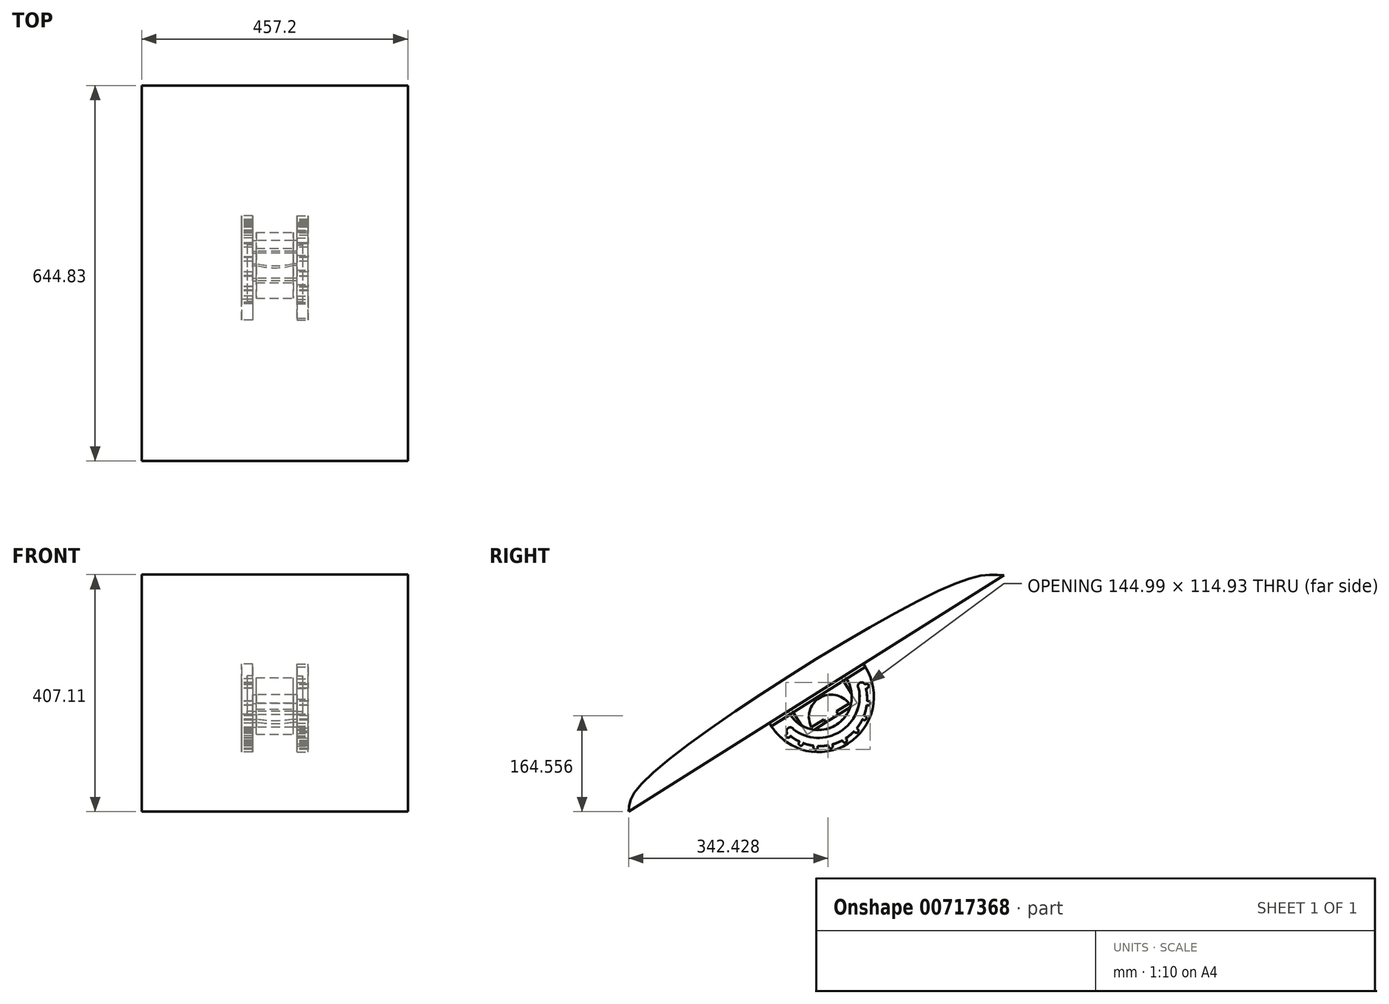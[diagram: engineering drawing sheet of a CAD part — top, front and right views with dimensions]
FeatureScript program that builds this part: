
annotation { "Feature Type Name" : "Feature", "Feature Type Description" : "" }
export const myFeature = defineFeature(function(context is Context, id is Id, definition is map)
    precondition{}
    {
        {
            var Q0;
            Q0=qCreatedBy(makeId("Right.planeOp"),FACE);
            var sketch = newSketch(context, id + "F0", { "sketchPlane" : qUnion([Q0])});
            skLineSegment(sketch, "E0", {"start": v(0, 0) * mm, "end": v(-644.83, -406) * mm});
            skFitSpline(sketch, "E1", {"points": [v(-644.83, -406) * mm, v(-622.98, -358.63) * mm, v(-89.62, -16.58) * mm, v(0, 0) * mm], "startDerivative": vector(4.72, 213.44) * mm, "endDerivative": vector(267.13, -25.02) * mm});
            skSolve(sketch);
        }
        {
            var Q0;
            Q0 = qSketchRegion(id + "F0", true);
            extrude(context, id + "F1", {"entities" : qUnion([Q0]), "depth" : 457.2 * mm, "offsetDistance" : 25.4 * mm});
        }
        {
            var Q0;
            Q0=makeQuery(id+"F1.opExtrude","SWEPT_FACE",FACE,{"disambiguationData":[OSD([sQuery(id+"F0.wireOp",EDGE,"E0")])]});
            var sketch = newSketch(context, id + "F2", { "sketchPlane" : qUnion([Q0])});
            skLineSegment(sketch, "E2", {"start": v(228.6, 0) * mm, "end": v(228.6, 762) * mm, "construction": true});
            skLineSegment(sketch, "E3", {"start": v(457.2, 381) * mm, "end": v(0, 381) * mm, "construction": true});
            skLineSegment(sketch, "E4.bottom", {"start": v(196.85, 431.8) * mm, "end": v(260.35, 431.8) * mm});
            skLineSegment(sketch, "E4.top", {"start": v(196.85, 330.2) * mm, "end": v(260.35, 330.2) * mm});
            skLineSegment(sketch, "E4.left", {"start": v(196.85, 431.8) * mm, "end": v(196.85, 330.2) * mm});
            skLineSegment(sketch, "E4.right", {"start": v(260.35, 431.8) * mm, "end": v(260.35, 330.2) * mm});
            skPoint(sketch, "E4.middle", {"position": v(228.6, 381) * mm});
            skSolve(sketch);
        }
        {
            var Q0;
            Q0=makeQuery(id+"F2.imprint","IMPRINT",FACE,{"disambiguationData":[TD([[makeQuery(id+"F2.imprint","IMPRINT",EDGE,{"derivedFrom":sQuery(id+"F2.wireOp",EDGE,"E4.bottom")}),-1.0]])]});
            extrude(context, id + "F3", {"entities" : qUnion([Q0]), "operationType" : NewBodyOperationType.ADD, "depth" : 50.8 * mm, "offsetDistance" : 25.4 * mm});
        }
        {
            var Q0;
            Q0=makeQuery(id+"F3.opExtrude","SWEPT_FACE",FACE,{"disambiguationData":[OSD([sQuery(id+"F2.wireOp",EDGE,"E4.left")])]});
            var sketch = newSketch(context, id + "F4", { "sketchPlane" : qUnion([Q0])});
            skLineSegment(sketch, "E5", {"start": v(252.36, -218.92) * mm, "end": v(284.6, -239.22) * mm, "construction": true});
            skLineSegment(sketch, "E6", {"start": v(338.34, -273.06) * mm, "end": v(306.1, -252.76) * mm, "construction": true});
            skLineSegment(sketch, "E7", {"start": v(284.6, -239.22) * mm, "end": v(306.1, -252.76) * mm});
            skLineSegment(sketch, "E8", {"start": v(306.1, -252.76) * mm, "end": v(309.48, -247.38) * mm});
            skLineSegment(sketch, "E9", {"start": v(284.6, -239.22) * mm, "end": v(287.98, -233.85) * mm});
            skLineSegment(sketch, "E10", {"start": v(309.48, -247.38) * mm, "end": v(330.97, -260.92) * mm});
            skLineSegment(sketch, "E11", {"start": v(287.98, -233.85) * mm, "end": v(266.49, -220.32) * mm});
            skArc(sketch, "E12", {"start": v(330.97, -260.92) * mm, "mid": v(317.44, -210.9) * mm, "end": v(266.49, -220.32) * mm});
            skSolve(sketch);
        }
        {
            var Q0;
            Q0=makeQuery(id+"F4.imprint","IMPRINT",FACE,{"disambiguationData":[TD([[makeQuery(id+"F4.imprint","IMPRINT",EDGE,{"derivedFrom":sQuery(id+"F4.wireOp",EDGE,"E7")}),-1.0]])]});
            extrude(context, id + "F5", {"entities" : qUnion([Q0]), "operationType" : NewBodyOperationType.REMOVE, "oppositeDirection" : true, "depth" : 127 * mm, "offsetDistance" : 25.4 * mm});
        }
        {
            var Q0;
            Q0=makeQuery(id+"F3.opExtrude","SWEPT_FACE",FACE,{"disambiguationData":[OSD([sQuery(id+"F2.wireOp",EDGE,"E4.left")])]});
            var sketch = newSketch(context, id + "F6", { "sketchPlane" : qUnion([Q0])});
            skLineSegment(sketch, "E13", {"start": v(284.6, -239.22) * mm, "end": v(306.1, -252.76) * mm});
            skSolve(sketch);
        }
        {
            var Q0;
            {var subQ1=sQuery(id+"F2.wireOp",EDGE,"E4.left");Q0=makeQuery(id+"F6.imprint","IMPRINT",FACE,{"disambiguationData":[TD([[makeQuery(id+"F6.imprint","IMPRINT",EDGE,{"derivedFrom":makeQuery(id+"F3.opExtrude","CAP_EDGE",EDGE,{"disambiguationData":[OSD([subQ1])],"isStart":true})}),1.0]])]});}
            var Q1;
            Q1=makeQuery(id+"F6.imprint","IMPRINT",FACE,{"disambiguationData":[TD([[makeQuery(id+"F6.imprint","IMPRINT",EDGE,{"derivedFrom":sQuery(id+"F6.wireOp",EDGE,"E13")}),1.0]])]});
            extrude(context, id + "F7", {"entities" : qUnion([Q0, Q1]), "operationType" : NewBodyOperationType.ADD, "depth" : 6.35 * mm, "offsetDistance" : 25.4 * mm});
        }
        {
            var Q0;
            Q0=makeQuery(id+"F3.opExtrude","SWEPT_FACE",FACE,{"disambiguationData":[OSD([sQuery(id+"F2.wireOp",EDGE,"E4.right")])]});
            var sketch = newSketch(context, id + "F8", { "sketchPlane" : qUnion([Q0])});
            skLineSegment(sketch, "E14", {"start": v(-306.1, -252.76) * mm, "end": v(-284.6, -239.22) * mm});
            skSolve(sketch);
        }
        {
            var Q0;
            {var subQ1=sQuery(id+"F2.wireOp",EDGE,"E4.right");Q0=makeQuery(id+"F8.imprint","IMPRINT",FACE,{"disambiguationData":[TD([[makeQuery(id+"F8.imprint","IMPRINT",EDGE,{"derivedFrom":makeQuery(id+"F3.opExtrude","CAP_EDGE",EDGE,{"disambiguationData":[OSD([subQ1])],"isStart":true})}),-1.0]])]});}
            var Q1;
            Q1=makeQuery(id+"F8.imprint","IMPRINT",FACE,{"disambiguationData":[TD([[makeQuery(id+"F8.imprint","IMPRINT",EDGE,{"derivedFrom":sQuery(id+"F8.wireOp",EDGE,"E14")}),1.0]])]});
            extrude(context, id + "F9", {"entities" : qUnion([Q0, Q1]), "operationType" : NewBodyOperationType.ADD, "depth" : 6.35 * mm, "offsetDistance" : 25.4 * mm});
        }
        {
            var Q0;
            {var subQ0=sQuery(id+"F2.wireOp",EDGE,"E4.right");var subQ1=sQuery(id+"F2.wireOp",EDGE,"E4.left");var subQ2=sQuery(id+"F2.wireOp",EDGE,"E4.top");var subQ5=sQuery(id+"F2.wireOp",EDGE,"E4.bottom");var subQ6=makeQuery(id+"F3.opExtrude","CAP_FACE",FACE,{"disambiguationData":[OSD([subQ5,subQ2,subQ1,subQ0])],"isStart":false});Q0=makeQuery(id+"F9.boolean.opBoolean","MERGE",FACE,{"derivedFrom":[makeQuery(id+"F7.boolean.opBoolean","MERGE",FACE,{"derivedFrom":[makeQuery(id+"F5.boolean.opBoolean","SPLIT",FACE,{"disambiguationData":[TD([makeQuery(id+"F3.opExtrude","SWEPT_FACE",FACE,{"disambiguationData":[OSD([subQ5])]})])],"derivedFrom":subQ6}),makeQuery(id+"F5.boolean.opBoolean","SPLIT",FACE,{"disambiguationData":[TD([makeQuery(id+"F3.opExtrude","SWEPT_FACE",FACE,{"disambiguationData":[OSD([subQ2])]})])],"derivedFrom":subQ6}),makeQuery(id+"F7.opExtrude","SWEPT_FACE",FACE,{"disambiguationData":[OSD([subQ1,sQuery(id+"F6.wireOp",EDGE,"E13")])]})]}),makeQuery(id+"F9.opExtrude","SWEPT_FACE",FACE,{"disambiguationData":[OSD([subQ0,sQuery(id+"F8.wireOp",EDGE,"E14")])]})]});}
            var sketch = newSketch(context, id + "F10", { "sketchPlane" : qUnion([Q0])});
            skArc(sketch, "E15", {"start": v(196.85, 368.3) * mm, "mid": v(228.6, 364.38) * mm, "end": v(260.35, 368.3) * mm});
            skArc(sketch, "E16", {"start": v(260.35, 393.7) * mm, "mid": v(228.6, 398.67) * mm, "end": v(196.85, 393.7) * mm});
            skSolve(sketch);
        }
        {
            var Q0;
            Q0=makeQuery(id+"F10.imprint","IMPRINT",FACE,{"disambiguationData":[TD([[makeQuery(id+"F10.imprint","IMPRINT",EDGE,{"derivedFrom":sQuery(id+"F10.wireOp",EDGE,"E15")}),1.0]])]});
            var Q1;
            Q1=makeQuery(id+"F10.imprint","IMPRINT",FACE,{"disambiguationData":[TD([[makeQuery(id+"F10.imprint","IMPRINT",EDGE,{"derivedFrom":sQuery(id+"F10.wireOp",EDGE,"E16")}),1.0]])]});
            extrude(context, id + "F11", {"entities" : qUnion([Q0, Q1]), "operationType" : NewBodyOperationType.REMOVE, "oppositeDirection" : true, "depth" : 7.62 * mm, "offsetDistance" : 25.4 * mm});
        }
        {
            var Q0;
            Q0=makeQuery(id+"F1.opExtrude","SWEPT_FACE",FACE,{"disambiguationData":[OSD([sQuery(id+"F0.wireOp",EDGE,"E0")])]});
            var sketch = newSketch(context, id + "F12", { "sketchPlane" : qUnion([Q0])});
            skLineSegment(sketch, "E17", {"start": v(266.7, 330.2) * mm, "end": v(266.7, 323.85) * mm, "construction": true});
            skLineSegment(sketch, "E18", {"start": v(266.7, 431.8) * mm, "end": v(266.7, 438.15) * mm, "construction": true});
            skLineSegment(sketch, "E19", {"start": v(190.5, 431.8) * mm, "end": v(190.5, 438.15) * mm, "construction": true});
            skLineSegment(sketch, "E20", {"start": v(190.5, 330.2) * mm, "end": v(190.5, 323.85) * mm, "construction": true});
            skLineSegment(sketch, "E21.bottom", {"start": v(266.7, 323.85) * mm, "end": v(285.75, 323.85) * mm});
            skLineSegment(sketch, "E21.top", {"start": v(266.7, 285.75) * mm, "end": v(285.75, 285.75) * mm});
            skLineSegment(sketch, "E21.left", {"start": v(266.7, 323.85) * mm, "end": v(266.7, 285.75) * mm});
            skLineSegment(sketch, "E21.right", {"start": v(285.75, 323.85) * mm, "end": v(285.75, 285.75) * mm});
            skLineSegment(sketch, "E22.bottom", {"start": v(190.5, 323.85) * mm, "end": v(171.45, 323.85) * mm});
            skLineSegment(sketch, "E22.top", {"start": v(190.5, 285.75) * mm, "end": v(171.45, 285.75) * mm});
            skLineSegment(sketch, "E22.left", {"start": v(190.5, 323.85) * mm, "end": v(190.5, 285.75) * mm});
            skLineSegment(sketch, "E22.right", {"start": v(171.45, 323.85) * mm, "end": v(171.45, 285.75) * mm});
            skLineSegment(sketch, "E23.bottom", {"start": v(266.7, 438.15) * mm, "end": v(285.75, 438.15) * mm});
            skLineSegment(sketch, "E23.top", {"start": v(266.7, 476.25) * mm, "end": v(285.75, 476.25) * mm});
            skLineSegment(sketch, "E23.left", {"start": v(266.7, 438.15) * mm, "end": v(266.7, 476.25) * mm});
            skLineSegment(sketch, "E23.right", {"start": v(285.75, 438.15) * mm, "end": v(285.75, 476.25) * mm});
            skPoint(sketch, "E24.oppositeSnap0", {"position": v(276.23, 476.25) * mm});
            skLineSegment(sketch, "E24.bottom", {"start": v(190.5, 438.15) * mm, "end": v(171.45, 438.15) * mm});
            skLineSegment(sketch, "E24.top", {"start": v(190.5, 476.25) * mm, "end": v(171.45, 476.25) * mm});
            skLineSegment(sketch, "E24.left", {"start": v(190.5, 438.15) * mm, "end": v(190.5, 476.25) * mm});
            skLineSegment(sketch, "E24.right", {"start": v(171.45, 438.15) * mm, "end": v(171.45, 476.25) * mm});
            skSolve(sketch);
        }
        {
            var Q0;
            Q0=makeQuery(id+"F12.imprint","IMPRINT",FACE,{"disambiguationData":[TD([[makeQuery(id+"F12.imprint","IMPRINT",EDGE,{"derivedFrom":sQuery(id+"F12.wireOp",EDGE,"E21.bottom")}),-1.0]])]});
            var Q1;
            Q1=makeQuery(id+"F12.imprint","IMPRINT",FACE,{"disambiguationData":[TD([[makeQuery(id+"F12.imprint","IMPRINT",EDGE,{"derivedFrom":sQuery(id+"F12.wireOp",EDGE,"E22.bottom")}),1.0]])]});
            var Q2;
            Q2=makeQuery(id+"F12.imprint","IMPRINT",FACE,{"disambiguationData":[TD([[makeQuery(id+"F12.imprint","IMPRINT",EDGE,{"derivedFrom":sQuery(id+"F12.wireOp",EDGE,"E24.bottom")}),-1.0]])]});
            var Q3;
            Q3=makeQuery(id+"F12.imprint","IMPRINT",FACE,{"disambiguationData":[TD([[makeQuery(id+"F12.imprint","IMPRINT",EDGE,{"derivedFrom":sQuery(id+"F12.wireOp",EDGE,"E23.bottom")}),1.0]])]});
            extrude(context, id + "F13", {"entities" : qUnion([Q0, Q1, Q2, Q3]), "operationType" : NewBodyOperationType.ADD, "depth" : 6.35 * mm, "offsetDistance" : 25.4 * mm});
        }
        {
            var Q0;
            Q0=makeQuery(id+"F1.opExtrude","SWEPT_FACE",FACE,{"disambiguationData":[OSD([sQuery(id+"F0.wireOp",EDGE,"E0")])]});
            var sketch = newSketch(context, id + "F14", { "sketchPlane" : qUnion([Q0])});
            skLineSegment(sketch, "E25", {"start": v(180.98, 323.85) * mm, "end": v(180.98, 438.15) * mm});
            skLineSegment(sketch, "E26", {"start": v(276.23, 323.85) * mm, "end": v(276.23, 438.15) * mm});
            skLineSegment(sketch, "E27", {"start": v(171.45, 438.15) * mm, "end": v(171.45, 323.85) * mm});
            skLineSegment(sketch, "E28", {"start": v(285.75, 438.15) * mm, "end": v(285.75, 323.85) * mm});
            skSolve(sketch);
        }
        {
            var Q0;
            {var subQ0=sQuery(id+"F14.wireOp",EDGE,"E26");Q0=makeQuery(id+"F14.imprint","IMPRINT",FACE,{"disambiguationData":[TD([[makeQuery(id+"F14.imprint","IMPRINT",EDGE,{"derivedFrom":subQ0}),-1.0]])]});}
            var Q1;
            {var subQ0=sQuery(id+"F14.wireOp",EDGE,"E25");Q1=makeQuery(id+"F14.imprint","IMPRINT",FACE,{"disambiguationData":[TD([[makeQuery(id+"F14.imprint","IMPRINT",EDGE,{"derivedFrom":subQ0}),1.0]])]});}
            extrude(context, id + "F15", {"entities" : qUnion([Q0, Q1]), "operationType" : NewBodyOperationType.ADD, "depth" : 6.35 * mm, "offsetDistance" : 25.4 * mm});
        }
        {
            var Q0;
            Q0=makeQuery(id+"F15.boolean.opBoolean","MERGE",FACE,{"derivedFrom":[makeQuery(id+"F13.opExtrude","SWEPT_FACE",FACE,{"disambiguationData":[OSD([sQuery(id+"F12.wireOp",EDGE,"E22.right")])]}),makeQuery(id+"F13.opExtrude","SWEPT_FACE",FACE,{"disambiguationData":[OSD([sQuery(id+"F12.wireOp",EDGE,"E24.right")])]}),makeQuery(id+"F15.opExtrude","SWEPT_FACE",FACE,{"disambiguationData":[OSD([sQuery(id+"F14.wireOp",EDGE,"E27")])]})]});
            var sketch = newSketch(context, id + "F16", { "sketchPlane" : qUnion([Q0])});
            skArc(sketch, "E29", {"start": v(270.41, -177.76) * mm, "mid": v(288.37, -256.78) * mm, "end": v(367.38, -238.82) * mm});
            skArc(sketch, "E30", {"start": v(238.43, -157.62) * mm, "mid": v(268.28, -288.98) * mm, "end": v(399.64, -259.13) * mm});
            skLineSegment(sketch, "E31", {"start": v(399.64, -259.13) * mm, "end": v(388.89, -252.36) * mm, "construction": true});
            skLineSegment(sketch, "E32", {"start": v(378.13, -245.59) * mm, "end": v(367.38, -238.82) * mm, "construction": true});
            skLineSegment(sketch, "E33", {"start": v(388.89, -252.36) * mm, "end": v(372.2, -271.52) * mm, "construction": true});
            skLineSegment(sketch, "E34", {"start": v(378.13, -245.59) * mm, "end": v(361.45, -264.74) * mm, "construction": true});
            skLineSegment(sketch, "E35", {"start": v(270.41, -177.76) * mm, "end": v(259.66, -171) * mm, "construction": true});
            skLineSegment(sketch, "E36", {"start": v(238.43, -157.62) * mm, "end": v(249.17, -164.4) * mm, "construction": true});
            skLineSegment(sketch, "E37", {"start": v(249.17, -164.4) * mm, "end": v(239.1, -187.71) * mm, "construction": true});
            skLineSegment(sketch, "E38", {"start": v(259.66, -171) * mm, "end": v(249.6, -194.32) * mm, "construction": true});
            skArc(sketch, "E39", {"start": v(249.6, -194.32) * mm, "mid": v(281.26, -268.07) * mm, "end": v(361.45, -264.74) * mm});
            skArc(sketch, "E40", {"start": v(239.1, -187.71) * mm, "mid": v(273.39, -280.87) * mm, "end": v(372.2, -271.52) * mm});
            skArc(sketch, "E41", {"start": v(372.2, -271.52) * mm, "mid": v(370.78, -261.85) * mm, "end": v(361.45, -264.74) * mm});
            skArc(sketch, "E42", {"start": v(249.6, -194.32) * mm, "mid": v(248.21, -184.89) * mm, "end": v(239.1, -187.71) * mm});
            skLineSegment(sketch, "E43", {"start": v(372.2, -271.52) * mm, "end": v(367.4, -275.66) * mm, "construction": true});
            skLineSegment(sketch, "E44", {"start": v(351.21, -285.7) * mm, "end": v(345.36, -288.17) * mm, "construction": true});
            skLineSegment(sketch, "E45", {"start": v(345.36, -288.17) * mm, "end": v(326.87, -292.74) * mm, "construction": true});
            skLineSegment(sketch, "E46", {"start": v(326.87, -292.74) * mm, "end": v(320.54, -293.29) * mm, "construction": true});
            skLineSegment(sketch, "E47", {"start": v(320.54, -293.29) * mm, "end": v(301.54, -291.95) * mm, "construction": true});
            skLineSegment(sketch, "E48", {"start": v(301.54, -291.95) * mm, "end": v(295.35, -290.52) * mm, "construction": true});
            skLineSegment(sketch, "E49", {"start": v(295.35, -290.52) * mm, "end": v(277.68, -283.4) * mm, "construction": true});
            skLineSegment(sketch, "E50", {"start": v(272.23, -280.13) * mm, "end": v(277.68, -283.4) * mm, "construction": true});
            skLineSegment(sketch, "E51", {"start": v(272.23, -280.13) * mm, "end": v(257.62, -267.91) * mm, "construction": true});
            skLineSegment(sketch, "E52", {"start": v(257.62, -267.91) * mm, "end": v(253.44, -263.13) * mm, "construction": true});
            skLineSegment(sketch, "E53", {"start": v(243.29, -247.01) * mm, "end": v(253.44, -263.13) * mm, "construction": true});
            skLineSegment(sketch, "E54", {"start": v(243.29, -247.01) * mm, "end": v(240.79, -241.18) * mm, "construction": true});
            skLineSegment(sketch, "E55", {"start": v(236.1, -222.71) * mm, "end": v(240.79, -241.18) * mm, "construction": true});
            skLineSegment(sketch, "E56", {"start": v(236.1, -222.71) * mm, "end": v(235.5, -216.4) * mm, "construction": true});
            skLineSegment(sketch, "E57", {"start": v(239.1, -187.71) * mm, "end": v(237.45, -193.84) * mm, "construction": true});
            skLineSegment(sketch, "E58", {"start": v(235.5, -216.4) * mm, "end": v(237.45, -193.84) * mm, "construction": true});
            skLineSegment(sketch, "E59", {"start": v(367.4, -275.66) * mm, "end": v(351.21, -285.7) * mm, "construction": true});
            skArc(sketch, "E60", {"start": v(367.4, -275.66) * mm, "mid": v(373.67, -278.07) * mm, "end": v(372.2, -271.52) * mm});
            skArc(sketch, "E61", {"start": v(345.36, -288.17) * mm, "mid": v(350.58, -292.39) * mm, "end": v(351.21, -285.7) * mm});
            skArc(sketch, "E62", {"start": v(320.54, -293.29) * mm, "mid": v(324.21, -298.9) * mm, "end": v(326.87, -292.74) * mm});
            skArc(sketch, "E63", {"start": v(295.35, -290.52) * mm, "mid": v(297.11, -297) * mm, "end": v(301.54, -291.95) * mm});
            skArc(sketch, "E64", {"start": v(272.23, -280.13) * mm, "mid": v(271.92, -286.84) * mm, "end": v(277.68, -283.4) * mm});
            skArc(sketch, "E65", {"start": v(253.44, -263.13) * mm, "mid": v(251.07, -269.42) * mm, "end": v(257.62, -267.91) * mm});
            skArc(sketch, "E66", {"start": v(240.79, -241.18) * mm, "mid": v(236.6, -246.43) * mm, "end": v(243.29, -247.01) * mm});
            skArc(sketch, "E67", {"start": v(235.5, -216.4) * mm, "mid": v(229.9, -220.1) * mm, "end": v(236.1, -222.71) * mm});
            skArc(sketch, "E68", {"start": v(239.1, -187.71) * mm, "mid": v(232.57, -189.23) * mm, "end": v(237.45, -193.84) * mm});
            skLineSegment(sketch, "E69", {"start": v(399.64, -259.13) * mm, "end": v(367.38, -238.82) * mm});
            skLineSegment(sketch, "E70", {"start": v(270.41, -177.76) * mm, "end": v(238.43, -157.62) * mm});
            skSolve(sketch);
        }
        {
            var Q0;
            Q0=makeQuery(id+"F16.imprint","IMPRINT",FACE,{"disambiguationData":[TD([[makeQuery(id+"F16.imprint","IMPRINT",EDGE,{"derivedFrom":sQuery(id+"F16.wireOp",EDGE,"E29")}),-1.0]])]});
            var Q1;
            Q1=makeQuery(id+"F7.opExtrude","CAP_FACE",FACE,{"disambiguationData":[OSD([sQuery(id+"F2.wireOp",EDGE,"E4.bottom"),sQuery(id+"F2.wireOp",EDGE,"E4.top"),sQuery(id+"F2.wireOp",EDGE,"E4.left"),sQuery(id+"F6.wireOp",EDGE,"E13")])],"isStart":false});
            var Q2;
            Q2=makeQuery(id+"F1.opExtrude","SWEPT_BODY",BODY,{"disambiguationData":[OSD([sQuery(id+"F0.wireOp",EDGE,"E0"),sQuery(id+"F0.wireOp",EDGE,"E1")])]});
            extrude(context, id + "F17", {"entities" : qUnion([Q0]), "operationType" : NewBodyOperationType.ADD, "endBound" : BoundingType.UP_TO_SURFACE, "oppositeDirection" : true, "depth" : 19.05 * mm, "endBoundEntityFace" : qUnion([Q1]), "endBoundEntityBody" : qUnion([Q2]), "offsetDistance" : 95.25 * mm, "offsetOppositeDirection" : true});
        }
        {
            var Q0;
            Q0=makeQuery(id+"F15.boolean.opBoolean","MERGE",FACE,{"derivedFrom":[makeQuery(id+"F13.opExtrude","SWEPT_FACE",FACE,{"disambiguationData":[OSD([sQuery(id+"F12.wireOp",EDGE,"E21.right")])]}),makeQuery(id+"F13.opExtrude","SWEPT_FACE",FACE,{"disambiguationData":[OSD([sQuery(id+"F12.wireOp",EDGE,"E23.right")])]}),makeQuery(id+"F15.opExtrude","SWEPT_FACE",FACE,{"disambiguationData":[OSD([sQuery(id+"F14.wireOp",EDGE,"E28")])]})]});
            var sketch = newSketch(context, id + "F18", { "sketchPlane" : qUnion([Q0])});
            skArc(sketch, "E71", {"start": v(-367.53, -239.07) * mm, "mid": v(-288.51, -257.01) * mm, "end": v(-270.57, -178) * mm});
            skArc(sketch, "E72", {"start": v(-399.51, -259.21) * mm, "mid": v(-268.15, -289.04) * mm, "end": v(-238.32, -157.69) * mm});
            skLineSegment(sketch, "E73", {"start": v(-238.32, -157.69) * mm, "end": v(-249.07, -164.45) * mm, "construction": true});
            skLineSegment(sketch, "E74", {"start": v(-259.82, -171.23) * mm, "end": v(-270.57, -178) * mm, "construction": true});
            skLineSegment(sketch, "E75", {"start": v(-249.07, -164.45) * mm, "end": v(-239, -187.77) * mm, "construction": true});
            skLineSegment(sketch, "E76", {"start": v(-259.82, -171.23) * mm, "end": v(-249.75, -194.55) * mm, "construction": true});
            skLineSegment(sketch, "E77", {"start": v(-367.53, -239.07) * mm, "end": v(-378.28, -245.84) * mm, "construction": true});
            skLineSegment(sketch, "E78", {"start": v(-399.51, -259.21) * mm, "end": v(-388.77, -252.44) * mm, "construction": true});
            skLineSegment(sketch, "E79", {"start": v(-388.77, -252.44) * mm, "end": v(-372.08, -271.6) * mm, "construction": true});
            skLineSegment(sketch, "E80", {"start": v(-378.28, -245.84) * mm, "end": v(-361.6, -265) * mm, "construction": true});
            skArc(sketch, "E81", {"start": v(-361.6, -265) * mm, "mid": v(-281.4, -268.31) * mm, "end": v(-249.75, -194.55) * mm});
            skArc(sketch, "E82", {"start": v(-372.08, -271.6) * mm, "mid": v(-273.26, -280.94) * mm, "end": v(-239, -187.77) * mm});
            skArc(sketch, "E83", {"start": v(-239, -187.77) * mm, "mid": v(-248.33, -184.88) * mm, "end": v(-249.75, -194.55) * mm});
            skArc(sketch, "E84", {"start": v(-361.6, -265) * mm, "mid": v(-370.7, -262.17) * mm, "end": v(-372.08, -271.6) * mm});
            skLineSegment(sketch, "E85", {"start": v(-239, -187.77) * mm, "end": v(-237.34, -193.9) * mm, "construction": true});
            skLineSegment(sketch, "E86", {"start": v(-235.27, -212.84) * mm, "end": v(-235.58, -219.18) * mm, "construction": true});
            skLineSegment(sketch, "E87", {"start": v(-235.58, -219.18) * mm, "end": v(-239.45, -237.84) * mm, "construction": true});
            skLineSegment(sketch, "E88", {"start": v(-239.45, -237.84) * mm, "end": v(-241.69, -243.78) * mm, "construction": true});
            skLineSegment(sketch, "E89", {"start": v(-241.69, -243.78) * mm, "end": v(-251.1, -260.34) * mm, "construction": true});
            skLineSegment(sketch, "E90", {"start": v(-251.1, -260.34) * mm, "end": v(-255.07, -265.3) * mm, "construction": true});
            skLineSegment(sketch, "E91", {"start": v(-255.07, -265.3) * mm, "end": v(-269.13, -278.15) * mm, "construction": true});
            skLineSegment(sketch, "E92", {"start": v(-274.43, -281.66) * mm, "end": v(-269.13, -278.15) * mm, "construction": true});
            skLineSegment(sketch, "E93", {"start": v(-274.43, -281.66) * mm, "end": v(-291.76, -289.56) * mm, "construction": true});
            skLineSegment(sketch, "E94", {"start": v(-291.76, -289.56) * mm, "end": v(-297.88, -291.26) * mm, "construction": true});
            skLineSegment(sketch, "E95", {"start": v(-316.8, -293.45) * mm, "end": v(-297.88, -291.26) * mm, "construction": true});
            skLineSegment(sketch, "E96", {"start": v(-316.8, -293.45) * mm, "end": v(-323.14, -293.19) * mm, "construction": true});
            skLineSegment(sketch, "E97", {"start": v(-341.82, -289.44) * mm, "end": v(-323.14, -293.19) * mm, "construction": true});
            skLineSegment(sketch, "E98", {"start": v(-341.82, -289.44) * mm, "end": v(-347.78, -287.24) * mm, "construction": true});
            skLineSegment(sketch, "E99", {"start": v(-372.08, -271.6) * mm, "end": v(-367.27, -275.74) * mm, "construction": true});
            skLineSegment(sketch, "E100", {"start": v(-347.78, -287.24) * mm, "end": v(-367.27, -275.74) * mm, "construction": true});
            skLineSegment(sketch, "E101", {"start": v(-237.34, -193.9) * mm, "end": v(-235.27, -212.84) * mm, "construction": true});
            skArc(sketch, "E102", {"start": v(-237.34, -193.9) * mm, "mid": v(-232.46, -189.29) * mm, "end": v(-239, -187.77) * mm});
            skArc(sketch, "E103", {"start": v(-235.58, -219.18) * mm, "mid": v(-229.52, -216.3) * mm, "end": v(-235.27, -212.84) * mm});
            skArc(sketch, "E104", {"start": v(-241.69, -243.78) * mm, "mid": v(-235.03, -242.9) * mm, "end": v(-239.45, -237.84) * mm});
            skArc(sketch, "E105", {"start": v(-255.07, -265.3) * mm, "mid": v(-248.47, -266.5) * mm, "end": v(-251.1, -260.34) * mm});
            skArc(sketch, "E106", {"start": v(-274.43, -281.66) * mm, "mid": v(-268.51, -284.84) * mm, "end": v(-269.13, -278.15) * mm});
            skArc(sketch, "E107", {"start": v(-297.88, -291.26) * mm, "mid": v(-293.23, -296.11) * mm, "end": v(-291.76, -289.56) * mm});
            skArc(sketch, "E108", {"start": v(-323.14, -293.19) * mm, "mid": v(-320.22, -299.23) * mm, "end": v(-316.8, -293.45) * mm});
            skArc(sketch, "E109", {"start": v(-347.78, -287.24) * mm, "mid": v(-346.85, -293.9) * mm, "end": v(-341.82, -289.44) * mm});
            skArc(sketch, "E110", {"start": v(-372.08, -271.6) * mm, "mid": v(-373.54, -278.15) * mm, "end": v(-367.27, -275.74) * mm});
            skLineSegment(sketch, "E111", {"start": v(-238.32, -157.69) * mm, "end": v(-270.57, -178) * mm});
            skLineSegment(sketch, "E112", {"start": v(-367.53, -239.07) * mm, "end": v(-399.51, -259.21) * mm});
            skSolve(sketch);
        }
        {
            var Q0;
            Q0=makeQuery(id+"F18.imprint","IMPRINT",FACE,{"disambiguationData":[TD([[makeQuery(id+"F18.imprint","IMPRINT",EDGE,{"derivedFrom":sQuery(id+"F18.wireOp",EDGE,"E71")}),-1.0]])]});
            extrude(context, id + "F19", {"entities" : qUnion([Q0]), "operationType" : NewBodyOperationType.ADD, "oppositeDirection" : true, "depth" : 19.05 * mm, "offsetDistance" : 25.4 * mm});
        }
        {
            var Q0;
            Q0=makeQuery(id+"F19.opExtrude","CAP_FACE",FACE,{"disambiguationData":[OSD([sQuery(id+"F18.wireOp",EDGE,"E71"),sQuery(id+"F18.wireOp",EDGE,"E72"),sQuery(id+"F18.wireOp",EDGE,"E81"),sQuery(id+"F18.wireOp",EDGE,"E82"),sQuery(id+"F18.wireOp",EDGE,"E83"),sQuery(id+"F18.wireOp",EDGE,"E84"),sQuery(id+"F18.wireOp",EDGE,"E102"),sQuery(id+"F18.wireOp",EDGE,"E103"),sQuery(id+"F18.wireOp",EDGE,"E104"),sQuery(id+"F18.wireOp",EDGE,"E105"),sQuery(id+"F18.wireOp",EDGE,"E106"),sQuery(id+"F18.wireOp",EDGE,"E107"),sQuery(id+"F18.wireOp",EDGE,"E108"),sQuery(id+"F18.wireOp",EDGE,"E109"),sQuery(id+"F18.wireOp",EDGE,"E110"),sQuery(id+"F18.wireOp",EDGE,"E111"),sQuery(id+"F18.wireOp",EDGE,"E112")])],"isStart":true});
            var sketch = newSketch(context, id + "F20", { "sketchPlane" : qUnion([Q0])});
            skLineSegment(sketch, "E113", {"start": v(-239, -187.77) * mm, "end": v(-237.34, -193.9) * mm});
            skLineSegment(sketch, "E114", {"start": v(-235.27, -212.84) * mm, "end": v(-235.58, -219.18) * mm});
            skLineSegment(sketch, "E115", {"start": v(-235.58, -219.18) * mm, "end": v(-239.45, -237.84) * mm});
            skLineSegment(sketch, "E116", {"start": v(-239.45, -237.84) * mm, "end": v(-241.69, -243.78) * mm});
            skLineSegment(sketch, "E117", {"start": v(-251.1, -260.34) * mm, "end": v(-255.07, -265.3) * mm});
            skLineSegment(sketch, "E118", {"start": v(-269.13, -278.15) * mm, "end": v(-274.43, -281.66) * mm});
            skLineSegment(sketch, "E119", {"start": v(-291.76, -289.56) * mm, "end": v(-297.88, -291.26) * mm});
            skLineSegment(sketch, "E120", {"start": v(-316.8, -293.45) * mm, "end": v(-323.14, -293.19) * mm});
            skLineSegment(sketch, "E121", {"start": v(-341.82, -289.44) * mm, "end": v(-347.78, -287.24) * mm});
            skSolve(sketch);
        }
        {
            var Q0;
            Q0=makeQuery(id+"F20.imprint","IMPRINT",FACE,{"disambiguationData":[TD([[makeQuery(id+"F20.imprint","IMPRINT",EDGE,{"derivedFrom":sQuery(id+"F20.wireOp",EDGE,"E113")}),1.0]])]});
            var Q1;
            Q1=makeQuery(id+"F20.imprint","IMPRINT",FACE,{"disambiguationData":[TD([[makeQuery(id+"F20.imprint","IMPRINT",EDGE,{"derivedFrom":sQuery(id+"F20.wireOp",EDGE,"E114")}),1.0]])]});
            var Q2;
            Q2=makeQuery(id+"F20.imprint","IMPRINT",FACE,{"disambiguationData":[TD([[makeQuery(id+"F20.imprint","IMPRINT",EDGE,{"derivedFrom":sQuery(id+"F20.wireOp",EDGE,"E116")}),1.0]])]});
            var Q3;
            Q3=makeQuery(id+"F20.imprint","IMPRINT",FACE,{"disambiguationData":[TD([[makeQuery(id+"F20.imprint","IMPRINT",EDGE,{"derivedFrom":sQuery(id+"F20.wireOp",EDGE,"E117")}),1.0]])]});
            var Q4;
            Q4=makeQuery(id+"F20.imprint","IMPRINT",FACE,{"disambiguationData":[TD([[makeQuery(id+"F20.imprint","IMPRINT",EDGE,{"derivedFrom":sQuery(id+"F20.wireOp",EDGE,"E118")}),1.0]])]});
            var Q5;
            Q5=makeQuery(id+"F20.imprint","IMPRINT",FACE,{"disambiguationData":[TD([[makeQuery(id+"F20.imprint","IMPRINT",EDGE,{"derivedFrom":sQuery(id+"F20.wireOp",EDGE,"E119")}),1.0]])]});
            var Q6;
            Q6=makeQuery(id+"F20.imprint","IMPRINT",FACE,{"disambiguationData":[TD([[makeQuery(id+"F20.imprint","IMPRINT",EDGE,{"derivedFrom":sQuery(id+"F20.wireOp",EDGE,"E120")}),1.0]])]});
            var Q7;
            Q7=makeQuery(id+"F20.imprint","IMPRINT",FACE,{"disambiguationData":[TD([[makeQuery(id+"F20.imprint","IMPRINT",EDGE,{"derivedFrom":sQuery(id+"F20.wireOp",EDGE,"E121")}),1.0]])]});
            extrude(context, id + "F21", {"entities" : qUnion([Q0, Q1, Q2, Q3, Q4, Q5, Q6, Q7]), "operationType" : NewBodyOperationType.ADD, "oppositeDirection" : true, "depth" : 19.05 * mm, "offsetDistance" : 25.4 * mm});
        }
        {
            var Q0;
            Q0=makeQuery(id+"F17.boolean.opBoolean","MERGE",FACE,{"derivedFrom":[makeQuery(id+"F15.boolean.opBoolean","MERGE",FACE,{"derivedFrom":[makeQuery(id+"F13.opExtrude","SWEPT_FACE",FACE,{"disambiguationData":[OSD([sQuery(id+"F12.wireOp",EDGE,"E22.right")])]}),makeQuery(id+"F13.opExtrude","SWEPT_FACE",FACE,{"disambiguationData":[OSD([sQuery(id+"F12.wireOp",EDGE,"E24.right")])]}),makeQuery(id+"F15.opExtrude","SWEPT_FACE",FACE,{"disambiguationData":[OSD([sQuery(id+"F14.wireOp",EDGE,"E27")])]})]}),makeQuery(id+"F17.opExtrude","CAP_FACE",FACE,{"disambiguationData":[OSD([sQuery(id+"F16.wireOp",EDGE,"E29"),sQuery(id+"F16.wireOp",EDGE,"E30"),sQuery(id+"F16.wireOp",EDGE,"E39"),sQuery(id+"F16.wireOp",EDGE,"E40"),sQuery(id+"F16.wireOp",EDGE,"E41"),sQuery(id+"F16.wireOp",EDGE,"E42"),sQuery(id+"F16.wireOp",EDGE,"E60"),sQuery(id+"F16.wireOp",EDGE,"E61"),sQuery(id+"F16.wireOp",EDGE,"E62"),sQuery(id+"F16.wireOp",EDGE,"E63"),sQuery(id+"F16.wireOp",EDGE,"E64"),sQuery(id+"F16.wireOp",EDGE,"E65"),sQuery(id+"F16.wireOp",EDGE,"E66"),sQuery(id+"F16.wireOp",EDGE,"E67"),sQuery(id+"F16.wireOp",EDGE,"E68"),sQuery(id+"F16.wireOp",EDGE,"E69"),sQuery(id+"F16.wireOp",EDGE,"E70")])],"isStart":true})]});
            var sketch = newSketch(context, id + "F22", { "sketchPlane" : qUnion([Q0])});
            skLineSegment(sketch, "E122", {"start": v(351.21, -285.7) * mm, "end": v(345.36, -288.17) * mm});
            skLineSegment(sketch, "E123", {"start": v(326.87, -292.74) * mm, "end": v(320.54, -293.29) * mm});
            skLineSegment(sketch, "E124", {"start": v(301.54, -291.95) * mm, "end": v(295.35, -290.52) * mm});
            skLineSegment(sketch, "E125", {"start": v(277.68, -283.4) * mm, "end": v(272.23, -280.13) * mm});
            skLineSegment(sketch, "E126", {"start": v(257.62, -267.91) * mm, "end": v(253.44, -263.13) * mm});
            skLineSegment(sketch, "E127", {"start": v(243.29, -247.01) * mm, "end": v(240.79, -241.18) * mm});
            skLineSegment(sketch, "E128", {"start": v(236.1, -222.71) * mm, "end": v(235.5, -216.4) * mm});
            skLineSegment(sketch, "E129", {"start": v(237.45, -193.84) * mm, "end": v(239.1, -187.71) * mm});
            skSolve(sketch);
        }
        {
            var Q0;
            Q0=makeQuery(id+"F22.imprint","IMPRINT",FACE,{"disambiguationData":[TD([[makeQuery(id+"F22.imprint","IMPRINT",EDGE,{"derivedFrom":sQuery(id+"F22.wireOp",EDGE,"E122")}),1.0]])]});
            var Q1;
            Q1=makeQuery(id+"F22.imprint","IMPRINT",FACE,{"disambiguationData":[TD([[makeQuery(id+"F22.imprint","IMPRINT",EDGE,{"derivedFrom":sQuery(id+"F22.wireOp",EDGE,"E123")}),1.0]])]});
            var Q2;
            Q2=makeQuery(id+"F22.imprint","IMPRINT",FACE,{"disambiguationData":[TD([[makeQuery(id+"F22.imprint","IMPRINT",EDGE,{"derivedFrom":sQuery(id+"F22.wireOp",EDGE,"E124")}),1.0]])]});
            var Q3;
            Q3=makeQuery(id+"F22.imprint","IMPRINT",FACE,{"disambiguationData":[TD([[makeQuery(id+"F22.imprint","IMPRINT",EDGE,{"derivedFrom":sQuery(id+"F22.wireOp",EDGE,"E125")}),1.0]])]});
            var Q4;
            Q4=makeQuery(id+"F22.imprint","IMPRINT",FACE,{"disambiguationData":[TD([[makeQuery(id+"F22.imprint","IMPRINT",EDGE,{"derivedFrom":sQuery(id+"F22.wireOp",EDGE,"E126")}),1.0]])]});
            var Q5;
            Q5=makeQuery(id+"F22.imprint","IMPRINT",FACE,{"disambiguationData":[TD([[makeQuery(id+"F22.imprint","IMPRINT",EDGE,{"derivedFrom":sQuery(id+"F22.wireOp",EDGE,"E127")}),1.0]])]});
            var Q6;
            Q6=makeQuery(id+"F22.imprint","IMPRINT",FACE,{"disambiguationData":[TD([[makeQuery(id+"F22.imprint","IMPRINT",EDGE,{"derivedFrom":sQuery(id+"F22.wireOp",EDGE,"E128")}),1.0]])]});
            var Q7;
            Q7=makeQuery(id+"F22.imprint","IMPRINT",FACE,{"disambiguationData":[TD([[makeQuery(id+"F22.imprint","IMPRINT",EDGE,{"derivedFrom":sQuery(id+"F22.wireOp",EDGE,"E129")}),1.0]])]});
            extrude(context, id + "F23", {"entities" : qUnion([Q0, Q1, Q2, Q3, Q4, Q5, Q6, Q7]), "operationType" : NewBodyOperationType.REMOVE, "oppositeDirection" : true, "depth" : 127 * mm, "offsetDistance" : 25.4 * mm});
        }
    });
